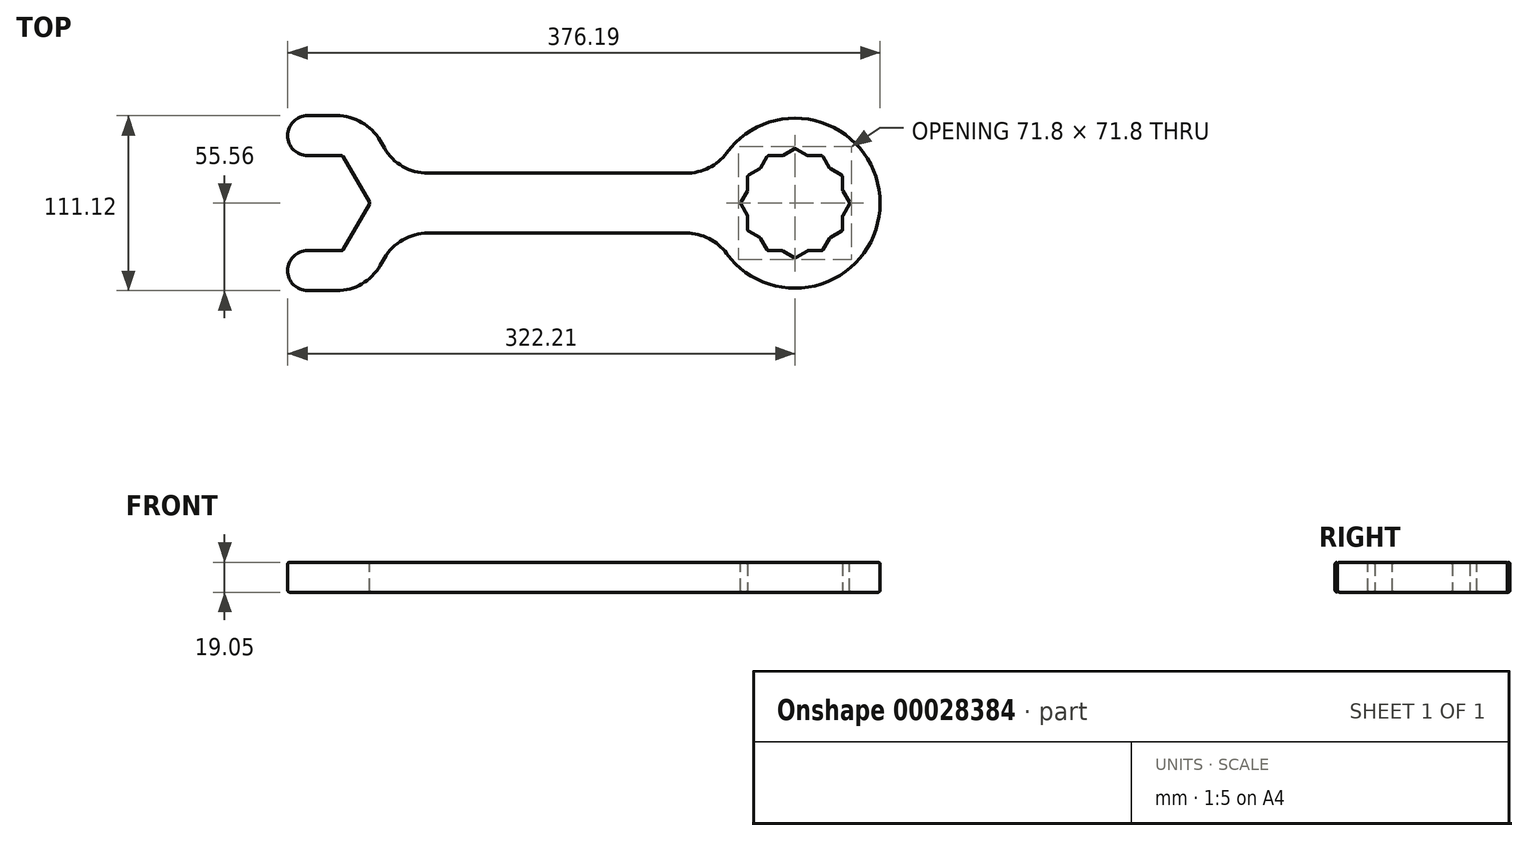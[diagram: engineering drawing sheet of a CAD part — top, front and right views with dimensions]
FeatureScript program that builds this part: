
annotation { "Feature Type Name" : "Feature", "Feature Type Description" : "" }
export const myFeature = defineFeature(function(context is Context, id is Id, definition is map)
    precondition{}
    {
        {
            var Q0;
            Q0=qCreatedBy(makeId("Top.planeOp"),FACE);
            var sketch = newSketch(context, id + "F0", { "sketchPlane" : qUnion([Q0])});
            skCircle(sketch, "E0.cCircle", {"center": v(0, 0) * mm, "radius": 30.16 * mm, "construction": true});
            skLineSegment(sketch, "E0.0", {"start": v(-17.41, 30.16) * mm, "end": v(17.41, 30.16) * mm});
            skLineSegment(sketch, "E0.1", {"start": v(17.41, 30.16) * mm, "end": v(34.83, 0) * mm});
            skLineSegment(sketch, "E0.2", {"start": v(34.83, 0) * mm, "end": v(17.41, -30.16) * mm});
            skLineSegment(sketch, "E0.3", {"start": v(17.41, -30.16) * mm, "end": v(-17.41, -30.16) * mm});
            skPoint(sketch, "E0.0.midPoint", {"position": v(0, 30.16) * mm});
            skCircle(sketch, "E1.cCircle", {"center": v(304.8, 0) * mm, "radius": 30.16 * mm, "construction": true});
            skLineSegment(sketch, "E1.0", {"start": v(287.39, 30.16) * mm, "end": v(296.72, 30.16) * mm});
            skLineSegment(sketch, "E1.1", {"start": v(322.21, 30.16) * mm, "end": v(326.88, 22.08) * mm});
            skLineSegment(sketch, "E1.3", {"start": v(322.21, -30.16) * mm, "end": v(312.88, -30.16) * mm});
            skLineSegment(sketch, "E1.4", {"start": v(287.39, -30.16) * mm, "end": v(282.72, -22.08) * mm});
            skLineSegment(sketch, "E1.5", {"start": v(269.97, 0) * mm, "end": v(274.64, 8.08) * mm});
            skPoint(sketch, "E1.0.midPoint", {"position": v(304.8, 30.16) * mm});
            skLineSegment(sketch, "E2.0", {"start": v(274.64, -17.41) * mm, "end": v(274.64, -8.08) * mm});
            skLineSegment(sketch, "E2.1", {"start": v(274.64, 17.41) * mm, "end": v(282.72, 22.08) * mm});
            skLineSegment(sketch, "E2.2", {"start": v(304.8, 34.83) * mm, "end": v(312.88, 30.16) * mm});
            skLineSegment(sketch, "E2.3", {"start": v(334.96, 17.41) * mm, "end": v(334.96, 8.08) * mm});
            skLineSegment(sketch, "E2.5", {"start": v(304.8, -34.83) * mm, "end": v(296.72, -30.16) * mm});
            skPoint(sketch, "E2.0.midPoint", {"position": v(274.64, 0) * mm});
            skArc(sketch, "E3", {"start": v(254.3, -19.05) * mm, "mid": v(358.78, 0) * mm, "end": v(254.3, 19.05) * mm});
            skLineSegment(sketch, "E4", {"start": v(-17.41, -30.16) * mm, "end": v(-17.41, -55.56) * mm});
            skLineSegment(sketch, "E5", {"start": v(-17.41, -55.56) * mm, "end": v(32.08, -55.56) * mm});
            skLineSegment(sketch, "E6", {"start": v(32.08, -55.56) * mm, "end": v(53.16, -19.05) * mm});
            skLineSegment(sketch, "E7", {"start": v(53.16, -19.05) * mm, "end": v(254.3, -19.05) * mm});
            skLineSegment(sketch, "E8", {"start": v(-17.41, 30.16) * mm, "end": v(-17.41, 55.56) * mm});
            skLineSegment(sketch, "E9", {"start": v(-17.41, 55.56) * mm, "end": v(32.08, 55.56) * mm});
            skLineSegment(sketch, "E10", {"start": v(32.08, 55.56) * mm, "end": v(53.16, 19.05) * mm});
            skLineSegment(sketch, "E11", {"start": v(53.16, 19.05) * mm, "end": v(254.3, 19.05) * mm});
            skLineSegment(sketch, "E12.trimOffspring", {"start": v(282.72, 22.08) * mm, "end": v(287.39, 30.16) * mm});
            skLineSegment(sketch, "E13.trimOffspring", {"start": v(274.64, 8.08) * mm, "end": v(274.64, 17.41) * mm});
            skLineSegment(sketch, "E14.trimOffspring", {"start": v(274.64, -8.08) * mm, "end": v(269.97, 0) * mm});
            skLineSegment(sketch, "E15.trimOffspring", {"start": v(282.72, -22.08) * mm, "end": v(274.64, -17.41) * mm});
            skLineSegment(sketch, "E16.trimOffspring", {"start": v(296.72, -30.16) * mm, "end": v(287.39, -30.16) * mm});
            skLineSegment(sketch, "E17.trimOffspring", {"start": v(312.88, -30.16) * mm, "end": v(304.8, -34.83) * mm});
            skLineSegment(sketch, "E18.trimOffspring", {"start": v(326.88, -22.08) * mm, "end": v(322.21, -30.16) * mm});
            skLineSegment(sketch, "E19", {"start": v(326.88, -22.08) * mm, "end": v(334.96, -17.41) * mm});
            skLineSegment(sketch, "E20", {"start": v(339.63, 0) * mm, "end": v(334.96, -8.08) * mm});
            skLineSegment(sketch, "E21.trimOffspring", {"start": v(334.96, -8.08) * mm, "end": v(334.96, -17.41) * mm});
            skLineSegment(sketch, "E22.trimOffspring", {"start": v(334.96, 8.08) * mm, "end": v(339.63, 0) * mm});
            skLineSegment(sketch, "E23.trimOffspring", {"start": v(326.88, 22.08) * mm, "end": v(334.96, 17.41) * mm});
            skLineSegment(sketch, "E24.trimOffspring", {"start": v(312.88, 30.16) * mm, "end": v(322.21, 30.16) * mm});
            skLineSegment(sketch, "E25.trimOffspring", {"start": v(296.72, 30.16) * mm, "end": v(304.8, 34.83) * mm});
            skSolve(sketch);
        }
        {
            var Q0;
            Q0 = qSketchRegion(id + "F0", true);
            extrude(context, id + "F1", {"entities" : qUnion([Q0]), "depth" : 19.05 * mm});
        }
        {
            var Q0;
            Q0=makeQuery(id+"F1.opExtrude","SWEPT_EDGE",EDGE,{"disambiguationData":[OSD([sQuery(id+"F0.wireOp",EDGE,"E10"),sQuery(id+"F0.wireOp",EDGE,"E11")])]});
            var Q1;
            Q1=makeQuery(id+"F1.opExtrude","SWEPT_EDGE",EDGE,{"disambiguationData":[OSD([sQuery(id+"F0.wireOp",EDGE,"E6"),sQuery(id+"F0.wireOp",EDGE,"E7")])]});
            var Q2;
            Q2=makeQuery(id+"F1.opExtrude","SWEPT_EDGE",EDGE,{"disambiguationData":[OSD([sQuery(id+"F0.wireOp",EDGE,"E3"),sQuery(id+"F0.wireOp",EDGE,"E11")])]});
            var Q3;
            Q3=makeQuery(id+"F1.opExtrude","SWEPT_EDGE",EDGE,{"disambiguationData":[OSD([sQuery(id+"F0.wireOp",EDGE,"E3"),sQuery(id+"F0.wireOp",EDGE,"E7")])]});
            var Q4;
            Q4=makeQuery(id+"F1.opExtrude","SWEPT_EDGE",EDGE,{"disambiguationData":[OSD([sQuery(id+"F0.wireOp",EDGE,"E5"),sQuery(id+"F0.wireOp",EDGE,"E6")])]});
            var Q5;
            Q5=makeQuery(id+"F1.opExtrude","SWEPT_EDGE",EDGE,{"disambiguationData":[OSD([sQuery(id+"F0.wireOp",EDGE,"E9"),sQuery(id+"F0.wireOp",EDGE,"E10")])]});
            fillet(context, id + "F2", {"entities" : qUnion([Q0, Q1, Q2, Q3, Q4, Q5]), "radius" : 31.75 * mm, "tangentPropagation" : true, "allowEdgeOverflow" : false});
        }
        {
            var Q0;
            Q0=makeQuery(id+"F1.opExtrude","SWEPT_EDGE",EDGE,{"disambiguationData":[OSD([sQuery(id+"F0.wireOp",EDGE,"E4"),sQuery(id+"F0.wireOp",EDGE,"E5")])]});
            var Q1;
            Q1=makeQuery(id+"F1.opExtrude","SWEPT_EDGE",EDGE,{"disambiguationData":[OSD([sQuery(id+"F0.wireOp",EDGE,"E0.3"),sQuery(id+"F0.wireOp",EDGE,"E4")])]});
            var Q2;
            Q2=makeQuery(id+"F1.opExtrude","SWEPT_EDGE",EDGE,{"disambiguationData":[OSD([sQuery(id+"F0.wireOp",EDGE,"E0.0"),sQuery(id+"F0.wireOp",EDGE,"E8")])]});
            var Q3;
            Q3=makeQuery(id+"F1.opExtrude","SWEPT_EDGE",EDGE,{"disambiguationData":[OSD([sQuery(id+"F0.wireOp",EDGE,"E8"),sQuery(id+"F0.wireOp",EDGE,"E9")])]});
            fillet(context, id + "F3", {"entities" : qUnion([Q0, Q1, Q2, Q3]), "radius" : 12.7 * mm, "tangentPropagation" : true, "allowEdgeOverflow" : false});
        }
        {
            var Q0;
            Q0=makeQuery(id+"F1.opExtrude","CAP_FACE",FACE,{"disambiguationData":[OSD([sQuery(id+"F0.wireOp",EDGE,"E0.0"),sQuery(id+"F0.wireOp",EDGE,"E0.1"),sQuery(id+"F0.wireOp",EDGE,"E0.2"),sQuery(id+"F0.wireOp",EDGE,"E0.3"),sQuery(id+"F0.wireOp",EDGE,"E1.0"),sQuery(id+"F0.wireOp",EDGE,"E1.1"),sQuery(id+"F0.wireOp",EDGE,"E1.3"),sQuery(id+"F0.wireOp",EDGE,"E1.4"),sQuery(id+"F0.wireOp",EDGE,"E1.5"),sQuery(id+"F0.wireOp",EDGE,"E2.0"),sQuery(id+"F0.wireOp",EDGE,"E2.1"),sQuery(id+"F0.wireOp",EDGE,"E2.2"),sQuery(id+"F0.wireOp",EDGE,"E2.3"),sQuery(id+"F0.wireOp",EDGE,"E2.5"),sQuery(id+"F0.wireOp",EDGE,"E3"),sQuery(id+"F0.wireOp",EDGE,"E4"),sQuery(id+"F0.wireOp",EDGE,"E5"),sQuery(id+"F0.wireOp",EDGE,"E6"),sQuery(id+"F0.wireOp",EDGE,"E7"),sQuery(id+"F0.wireOp",EDGE,"E8"),sQuery(id+"F0.wireOp",EDGE,"E9"),sQuery(id+"F0.wireOp",EDGE,"E10"),sQuery(id+"F0.wireOp",EDGE,"E11"),sQuery(id+"F0.wireOp",EDGE,"E12.trimOffspring"),sQuery(id+"F0.wireOp",EDGE,"E13.trimOffspring"),sQuery(id+"F0.wireOp",EDGE,"E14.trimOffspring"),sQuery(id+"F0.wireOp",EDGE,"E15.trimOffspring"),sQuery(id+"F0.wireOp",EDGE,"E16.trimOffspring"),sQuery(id+"F0.wireOp",EDGE,"E17.trimOffspring"),sQuery(id+"F0.wireOp",EDGE,"E18.trimOffspring"),sQuery(id+"F0.wireOp",EDGE,"E19"),sQuery(id+"F0.wireOp",EDGE,"E20"),sQuery(id+"F0.wireOp",EDGE,"E21.trimOffspring"),sQuery(id+"F0.wireOp",EDGE,"E22.trimOffspring"),sQuery(id+"F0.wireOp",EDGE,"E23.trimOffspring"),sQuery(id+"F0.wireOp",EDGE,"E24.trimOffspring"),sQuery(id+"F0.wireOp",EDGE,"E25.trimOffspring")])],"isStart":true});
            var Q1;
            Q1=makeQuery(id+"F1.opExtrude","CAP_FACE",FACE,{"disambiguationData":[OSD([sQuery(id+"F0.wireOp",EDGE,"E0.0"),sQuery(id+"F0.wireOp",EDGE,"E0.1"),sQuery(id+"F0.wireOp",EDGE,"E0.2"),sQuery(id+"F0.wireOp",EDGE,"E0.3"),sQuery(id+"F0.wireOp",EDGE,"E1.0"),sQuery(id+"F0.wireOp",EDGE,"E1.1"),sQuery(id+"F0.wireOp",EDGE,"E1.3"),sQuery(id+"F0.wireOp",EDGE,"E1.4"),sQuery(id+"F0.wireOp",EDGE,"E1.5"),sQuery(id+"F0.wireOp",EDGE,"E2.0"),sQuery(id+"F0.wireOp",EDGE,"E2.1"),sQuery(id+"F0.wireOp",EDGE,"E2.2"),sQuery(id+"F0.wireOp",EDGE,"E2.3"),sQuery(id+"F0.wireOp",EDGE,"E2.5"),sQuery(id+"F0.wireOp",EDGE,"E3"),sQuery(id+"F0.wireOp",EDGE,"E4"),sQuery(id+"F0.wireOp",EDGE,"E5"),sQuery(id+"F0.wireOp",EDGE,"E6"),sQuery(id+"F0.wireOp",EDGE,"E7"),sQuery(id+"F0.wireOp",EDGE,"E8"),sQuery(id+"F0.wireOp",EDGE,"E9"),sQuery(id+"F0.wireOp",EDGE,"E10"),sQuery(id+"F0.wireOp",EDGE,"E11"),sQuery(id+"F0.wireOp",EDGE,"E12.trimOffspring"),sQuery(id+"F0.wireOp",EDGE,"E13.trimOffspring"),sQuery(id+"F0.wireOp",EDGE,"E14.trimOffspring"),sQuery(id+"F0.wireOp",EDGE,"E15.trimOffspring"),sQuery(id+"F0.wireOp",EDGE,"E16.trimOffspring"),sQuery(id+"F0.wireOp",EDGE,"E17.trimOffspring"),sQuery(id+"F0.wireOp",EDGE,"E18.trimOffspring"),sQuery(id+"F0.wireOp",EDGE,"E19"),sQuery(id+"F0.wireOp",EDGE,"E20"),sQuery(id+"F0.wireOp",EDGE,"E21.trimOffspring"),sQuery(id+"F0.wireOp",EDGE,"E22.trimOffspring"),sQuery(id+"F0.wireOp",EDGE,"E23.trimOffspring"),sQuery(id+"F0.wireOp",EDGE,"E24.trimOffspring"),sQuery(id+"F0.wireOp",EDGE,"E25.trimOffspring")])],"isStart":false});
            var Q2;
            Q2=makeQuery(id+"F1.opExtrude","SWEPT_FACE",FACE,{"disambiguationData":[OSD([sQuery(id+"F0.wireOp",EDGE,"E0.2")])]});
            var Q3;
            Q3=makeQuery(id+"F1.opExtrude","SWEPT_FACE",FACE,{"disambiguationData":[OSD([sQuery(id+"F0.wireOp",EDGE,"E0.1")])]});
            var Q4;
            Q4=makeQuery(id+"F1.opExtrude","SWEPT_FACE",FACE,{"disambiguationData":[OSD([sQuery(id+"F0.wireOp",EDGE,"E2.3")])]});
            var Q5;
            Q5=makeQuery(id+"F1.opExtrude","SWEPT_FACE",FACE,{"disambiguationData":[OSD([sQuery(id+"F0.wireOp",EDGE,"E1.1")])]});
            var Q6;
            Q6=makeQuery(id+"F1.opExtrude","SWEPT_EDGE",EDGE,{"disambiguationData":[OSD([sQuery(id+"F0.wireOp",EDGE,"E2.2"),sQuery(id+"F0.wireOp",EDGE,"E24.trimOffspring")])]});
            var Q7;
            Q7=makeQuery(id+"F1.opExtrude","SWEPT_FACE",FACE,{"disambiguationData":[OSD([sQuery(id+"F0.wireOp",EDGE,"E25.trimOffspring")])]});
            var Q8;
            Q8=makeQuery(id+"F1.opExtrude","SWEPT_FACE",FACE,{"disambiguationData":[OSD([sQuery(id+"F0.wireOp",EDGE,"E12.trimOffspring")])]});
            var Q9;
            Q9=makeQuery(id+"F1.opExtrude","SWEPT_FACE",FACE,{"disambiguationData":[OSD([sQuery(id+"F0.wireOp",EDGE,"E1.5")])]});
            var Q10;
            Q10=makeQuery(id+"F1.opExtrude","SWEPT_FACE",FACE,{"disambiguationData":[OSD([sQuery(id+"F0.wireOp",EDGE,"E20")])]});
            var Q11;
            Q11=makeQuery(id+"F1.opExtrude","SWEPT_FACE",FACE,{"disambiguationData":[OSD([sQuery(id+"F0.wireOp",EDGE,"E2.0")])]});
            var Q12;
            Q12=makeQuery(id+"F1.opExtrude","SWEPT_FACE",FACE,{"disambiguationData":[OSD([sQuery(id+"F0.wireOp",EDGE,"E1.4")])]});
            var Q13;
            Q13=makeQuery(id+"F1.opExtrude","SWEPT_FACE",FACE,{"disambiguationData":[OSD([sQuery(id+"F0.wireOp",EDGE,"E2.5")])]});
            var Q14;
            Q14=makeQuery(id+"F1.opExtrude","SWEPT_FACE",FACE,{"disambiguationData":[OSD([sQuery(id+"F0.wireOp",EDGE,"E19")])]});
            var Q15;
            Q15=makeQuery(id+"F1.opExtrude","SWEPT_FACE",FACE,{"disambiguationData":[OSD([sQuery(id+"F0.wireOp",EDGE,"E1.3")])]});
            var Q16;
            Q16=makeQuery(id+"F1.opExtrude","SWEPT_EDGE",EDGE,{"disambiguationData":[OSD([sQuery(id+"F0.wireOp",EDGE,"E2.1"),sQuery(id+"F0.wireOp",EDGE,"E13.trimOffspring")])]});
            fillet(context, id + "F4", {"entities" : qUnion([Q0, Q1, Q2, Q3, Q4, Q5, Q6, Q7, Q8, Q9, Q10, Q11, Q12, Q13, Q14, Q15, Q16]), "radius" : 1.27 * mm, "tangentPropagation" : true, "allowEdgeOverflow" : false});
        }
    });
